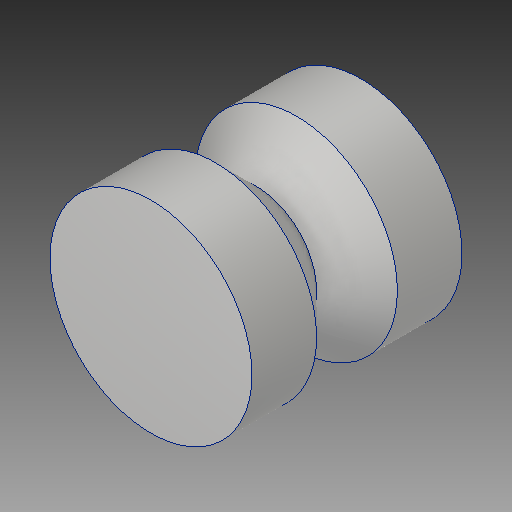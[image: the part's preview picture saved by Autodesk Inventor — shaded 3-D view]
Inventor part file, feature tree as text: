
AUTODESK INVENTOR PART (.ipt)
format: ipt  version: 2019 (Build 230136000, 136)  size: 122,368 bytes
history: native  units: in
note: dims shown in document units (in); Inventor stores cm internally (conversion verified against a paired STEP export)
features: extrude x2, chamfer x2, sketch x2
ambient origin geometry x8: Origin, YZ Plane, XZ Plane, XY Plane, X Axis, Y Axis, Z Axis, Center Point
bodies: Solid1 (feature_tree)
feature tree (6):
  extrude  "Extrusion1"  Depth=0.26in TaperAngle=0.0deg
  chamfer  "Chamfer1"  Distance=0.1in Angle=45.0deg
  extrude  "Extrusion2"  Depth=0.26in TaperAngle=0.0deg
  chamfer  "Chamfer2"  Distance=0.1in Angle=45.0deg
  sketch  "Sketch1"  dims[d0=0.5in d1=0.26in d2=0.0in d3=0.1in d4=0.125in d5=45.0deg]
  sketch  "Sketch2"  dims[d6=0.5in d7=0.26in d8=0.0in d9=0.1in d10=0.125in d11=45.0deg]
